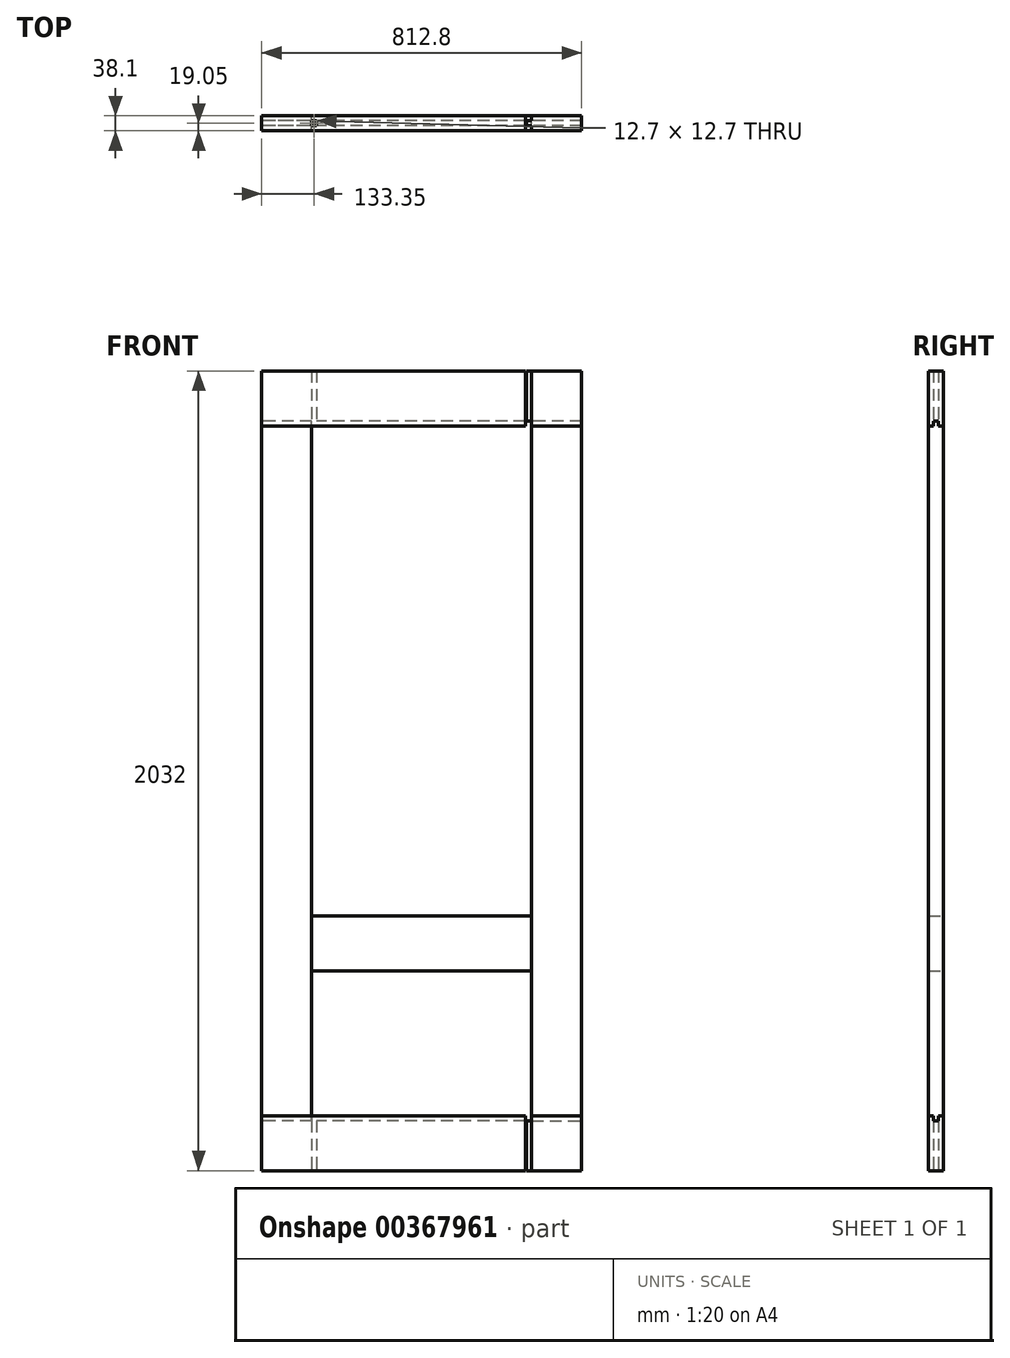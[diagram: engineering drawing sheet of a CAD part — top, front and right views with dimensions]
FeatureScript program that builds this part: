
annotation { "Feature Type Name" : "Feature", "Feature Type Description" : "" }
export const myFeature = defineFeature(function(context is Context, id is Id, definition is map)
    precondition{}
    {
        {
            var Q0;
            Q0=qCreatedBy(makeId("Right.planeOp"),FACE);
            var sketch = newSketch(context, id + "F0", { "sketchPlane" : qUnion([Q0])});
            skLineSegment(sketch, "E0", {"start": v(0, 0) * mm, "end": v(0, 139.7) * mm});
            skLineSegment(sketch, "E1", {"start": v(0, 139.7) * mm, "end": v(12.7, 139.7) * mm});
            skLineSegment(sketch, "E2", {"start": v(25.4, 139.7) * mm, "end": v(38.1, 139.7) * mm});
            skLineSegment(sketch, "E3", {"start": v(38.1, 139.7) * mm, "end": v(38.1, 0) * mm});
            skLineSegment(sketch, "E4", {"start": v(38.1, 0) * mm, "end": v(0, 0) * mm});
            skLineSegment(sketch, "E5", {"start": v(12.7, 139.7) * mm, "end": v(12.7, 127) * mm});
            skLineSegment(sketch, "E6", {"start": v(25.4, 139.7) * mm, "end": v(25.4, 127) * mm});
            skLineSegment(sketch, "E7", {"start": v(12.7, 127) * mm, "end": v(25.4, 127) * mm});
            skSolve(sketch);
        }
        {
            var Q0;
            Q0 = qSketchRegion(id + "F0", true);
            extrude(context, id + "F1", {"entities" : qUnion([Q0]), "depth" : 812.8 * mm});
        }
        {
            var Q0;
            Q0=qCreatedBy(makeId("Top.planeOp"),FACE);
            cPlane(context, id + "F2", {"entities" : qUnion([Q0]), "cplaneType" : CPlaneType.OFFSET, "offset" : 1016 * mm, "width" : 152.4 * mm, "height" : 152.4 * mm});
        }
        {
            var Q0;
            Q0=makeQuery(id+"F1.opExtrude","SWEPT_BODY",BODY,{"disambiguationData":[OSD([sQuery(id+"F0.wireOp",EDGE,"E0"),sQuery(id+"F0.wireOp",EDGE,"E1"),sQuery(id+"F0.wireOp",EDGE,"E2"),sQuery(id+"F0.wireOp",EDGE,"E3"),sQuery(id+"F0.wireOp",EDGE,"E4"),sQuery(id+"F0.wireOp",EDGE,"E5"),sQuery(id+"F0.wireOp",EDGE,"E6"),sQuery(id+"F0.wireOp",EDGE,"E7")])]});
            var Q1;
            Q1=qCreatedBy(id+"F2.planeOp",FACE);
            mirror(context, id + "F3", {"entities" : qUnion([Q0]), "mirrorPlane" : qUnion([Q1])});
        }
        {
            var Q0;
            Q0=qCreatedBy(makeId("Right.planeOp"),FACE);
            var sketch = newSketch(context, id + "F4", { "sketchPlane" : qUnion([Q0])});
            skLineSegment(sketch, "E8", {"start": v(0, 139.7) * mm, "end": v(12.7, 139.7) * mm});
            skLineSegment(sketch, "E9", {"start": v(12.7, 139.7) * mm, "end": v(12.7, 127) * mm});
            skLineSegment(sketch, "E10", {"start": v(12.7, 127) * mm, "end": v(25.4, 127) * mm});
            skLineSegment(sketch, "E11", {"start": v(25.4, 127) * mm, "end": v(25.4, 139.52) * mm});
            skLineSegment(sketch, "E12", {"start": v(25.4, 139.52) * mm, "end": v(38.1, 139.52) * mm});
            skLineSegment(sketch, "E13", {"start": v(38.1, 139.52) * mm, "end": v(38.1, 1892.3) * mm});
            skLineSegment(sketch, "E14", {"start": v(38.1, 1892.3) * mm, "end": v(25.4, 1892.3) * mm});
            skLineSegment(sketch, "E15", {"start": v(25.4, 1892.3) * mm, "end": v(25.4, 1905) * mm});
            skLineSegment(sketch, "E16", {"start": v(25.4, 1905) * mm, "end": v(12.7, 1905) * mm});
            skLineSegment(sketch, "E17", {"start": v(12.7, 1905) * mm, "end": v(12.7, 1892.3) * mm});
            skLineSegment(sketch, "E18", {"start": v(12.7, 1892.3) * mm, "end": v(0, 1892.3) * mm});
            skLineSegment(sketch, "E19", {"start": v(0, 1892.3) * mm, "end": v(0, 139.7) * mm});
            skSolve(sketch);
        }
        {
            var Q0;
            Q0 = qSketchRegion(id + "F4", true);
            extrude(context, id + "F5", {"entities" : qUnion([Q0]), "depth" : 127 * mm});
        }
        {
            var Q0;
            Q0=qCreatedBy(makeId("Right.planeOp"),FACE);
            cPlane(context, id + "F6", {"entities" : qUnion([Q0]), "cplaneType" : CPlaneType.OFFSET, "offset" : 406.4 * mm, "width" : 152.4 * mm, "height" : 152.4 * mm});
        }
        {
            var Q0;
            Q0=makeQuery(id+"F5.opExtrude","SWEPT_BODY",BODY,{"disambiguationData":[OSD([sQuery(id+"F4.wireOp",EDGE,"E8"),sQuery(id+"F4.wireOp",EDGE,"E9"),sQuery(id+"F4.wireOp",EDGE,"E10"),sQuery(id+"F4.wireOp",EDGE,"E11"),sQuery(id+"F4.wireOp",EDGE,"E12"),sQuery(id+"F4.wireOp",EDGE,"E13"),sQuery(id+"F4.wireOp",EDGE,"E14"),sQuery(id+"F4.wireOp",EDGE,"E15"),sQuery(id+"F4.wireOp",EDGE,"E16"),sQuery(id+"F4.wireOp",EDGE,"E17"),sQuery(id+"F4.wireOp",EDGE,"E18"),sQuery(id+"F4.wireOp",EDGE,"E19")])]});
            var Q1;
            Q1=qCreatedBy(id+"F6.planeOp",FACE);
            mirror(context, id + "F7", {"entities" : qUnion([Q0]), "mirrorPlane" : qUnion([Q1])});
        }
        {
            var Q0;
            Q0=qCreatedBy(makeId("Top.planeOp"),FACE);
            var sketch = newSketch(context, id + "F8", { "sketchPlane" : qUnion([Q0])});
            skLineSegment(sketch, "E20", {"start": v(669.93, 38.1) * mm, "end": v(685.8, 38.1) * mm});
            skLineSegment(sketch, "E21", {"start": v(685.8, 38.1) * mm, "end": v(685.8, 25.4) * mm});
            skLineSegment(sketch, "E22", {"start": v(685.8, 25.4) * mm, "end": v(673.1, 25.4) * mm});
            skLineSegment(sketch, "E23", {"start": v(673.1, 25.4) * mm, "end": v(673.1, 12.7) * mm});
            skLineSegment(sketch, "E24", {"start": v(673.1, 12.7) * mm, "end": v(685.8, 12.7) * mm});
            skLineSegment(sketch, "E25", {"start": v(685.8, 12.7) * mm, "end": v(685.8, 0) * mm});
            skLineSegment(sketch, "E26", {"start": v(685.8, 0) * mm, "end": v(669.93, 0) * mm});
            skLineSegment(sketch, "E27", {"start": v(669.93, 38.1) * mm, "end": v(669.93, 0) * mm});
            skSolve(sketch);
        }
        {
            var Q0;
            Q0 = qSketchRegion(id + "F8", true);
            extrude(context, id + "F9", {"entities" : qUnion([Q0]), "operationType" : NewBodyOperationType.REMOVE, "endBound" : BoundingType.THROUGH_ALL, "depth" : 25.4 * mm});
        }
        {
            var Q0;
            Q0=qCreatedBy(makeId("Top.planeOp"),FACE);
            var sketch = newSketch(context, id + "F10", { "sketchPlane" : qUnion([Q0])});
            skLineSegment(sketch, "E28", {"start": v(139.7, 25.4) * mm, "end": v(127, 25.4) * mm});
            skLineSegment(sketch, "E29", {"start": v(127, 25.4) * mm, "end": v(127, 12.7) * mm});
            skLineSegment(sketch, "E30", {"start": v(127, 12.7) * mm, "end": v(139.7, 12.7) * mm});
            skLineSegment(sketch, "E31", {"start": v(139.7, 25.4) * mm, "end": v(139.7, 12.7) * mm});
            skSolve(sketch);
        }
        {
            var Q0;
            Q0 = qSketchRegion(id + "F10", true);
            extrude(context, id + "F11", {"entities" : qUnion([Q0]), "operationType" : NewBodyOperationType.REMOVE, "endBound" : BoundingType.THROUGH_ALL, "depth" : 25.4 * mm});
        }
        {
            var Q0;
            Q0=qCreatedBy(id+"F6.planeOp",FACE);
            var sketch = newSketch(context, id + "F12", { "sketchPlane" : qUnion([Q0])});
            skLineSegment(sketch, "E32.bottom", {"start": v(0, 508) * mm, "end": v(38.1, 508) * mm});
            skLineSegment(sketch, "E32.top", {"start": v(0, 647.7) * mm, "end": v(38.1, 647.7) * mm});
            skLineSegment(sketch, "E32.left", {"start": v(0, 508) * mm, "end": v(0, 647.7) * mm});
            skLineSegment(sketch, "E32.right", {"start": v(38.1, 508) * mm, "end": v(38.1, 647.7) * mm});
            skSolve(sketch);
        }
        {
            var Q0;
            Q0 = qSketchRegion(id + "F12", true);
            extrude(context, id + "F13", {"entities" : qUnion([Q0]), "endBound" : BoundingType.SYMMETRIC, "depth" : 558.8 * mm});
        }
    });
